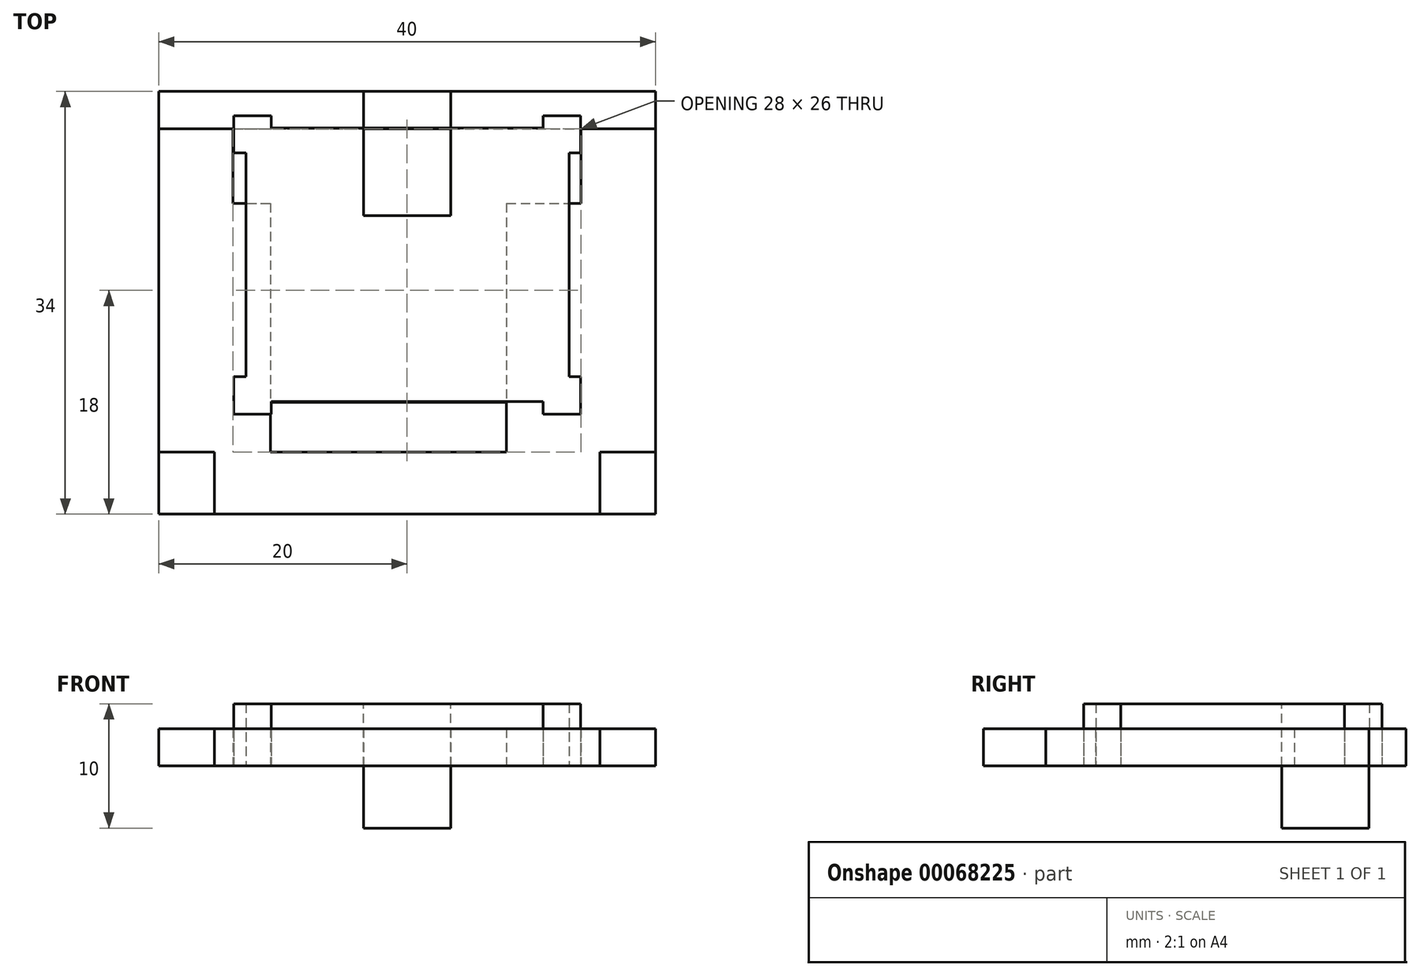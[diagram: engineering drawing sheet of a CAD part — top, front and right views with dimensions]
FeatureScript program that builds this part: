
annotation { "Feature Type Name" : "Feature", "Feature Type Description" : "" }
export const myFeature = defineFeature(function(context is Context, id is Id, definition is map)
    precondition{}
    {
        {
            var Q0;
            Q0=qCreatedBy(makeId("Top.planeOp"),FACE);
            var sketch = newSketch(context, id + "F0", { "sketchPlane" : qUnion([Q0])});
            skLineSegment(sketch, "E0.rect.bottom", {"start": v(-20, 17) * mm, "end": v(20, 17) * mm});
            skLineSegment(sketch, "E0.rect.top", {"start": v(-20, -17) * mm, "end": v(20, -17) * mm});
            skLineSegment(sketch, "E0.rect.left", {"start": v(-20, 17) * mm, "end": v(-20, -17) * mm});
            skLineSegment(sketch, "E0.rect.right", {"start": v(20, 17) * mm, "end": v(20, -17) * mm});
            skPoint(sketch, "E0.rect.middle", {"position": v(0, 0) * mm});
            skLineSegment(sketch, "E1.bottom", {"start": v(-20, -17) * mm, "end": v(-15.5, -17) * mm});
            skLineSegment(sketch, "E1.top", {"start": v(-20, -12) * mm, "end": v(-15.5, -12) * mm});
            skLineSegment(sketch, "E1.left", {"start": v(-20, -17) * mm, "end": v(-20, -12) * mm});
            skLineSegment(sketch, "E1.right", {"start": v(-15.5, -17) * mm, "end": v(-15.5, -12) * mm});
            skLineSegment(sketch, "E2.MirrorCS", {"start": v(15.5, -17) * mm, "end": v(15.5, -12) * mm});
            skLineSegment(sketch, "E3.MirrorCS", {"start": v(20, -17) * mm, "end": v(20, -12) * mm});
            skLineSegment(sketch, "E4.MirrorCS", {"start": v(20, -17) * mm, "end": v(15.5, -17) * mm});
            skLineSegment(sketch, "E5.MirrorCS", {"start": v(20, -12) * mm, "end": v(15.5, -12) * mm});
            skLineSegment(sketch, "E6.bottom", {"start": v(-20, 17) * mm, "end": v(-14, 17) * mm});
            skLineSegment(sketch, "E6.top", {"start": v(-20, 14) * mm, "end": v(-14, 14) * mm});
            skLineSegment(sketch, "E6.left", {"start": v(-20, 17) * mm, "end": v(-20, 14) * mm});
            skLineSegment(sketch, "E6.right", {"start": v(-14, 17) * mm, "end": v(-14, 14) * mm});
            skLineSegment(sketch, "E7.MirrorCS", {"start": v(20, 17) * mm, "end": v(20, 14) * mm});
            skLineSegment(sketch, "E8.MirrorCS", {"start": v(14, 17) * mm, "end": v(14, 14) * mm});
            skLineSegment(sketch, "E9.MirrorCS", {"start": v(20, 14) * mm, "end": v(14, 14) * mm});
            skLineSegment(sketch, "E10.MirrorCS", {"start": v(20, 17) * mm, "end": v(14, 17) * mm});
            skLineSegment(sketch, "E11.MirrorCS", {"start": v(20, 17) * mm, "end": v(-20, 17) * mm});
            skLineSegment(sketch, "E12.bottom", {"start": v(-14, 14) * mm, "end": v(14, 14) * mm});
            skLineSegment(sketch, "E12.top", {"start": v(-14, -12) * mm, "end": v(14, -12) * mm});
            skLineSegment(sketch, "E12.left", {"start": v(-14, 14) * mm, "end": v(-14, -12) * mm});
            skLineSegment(sketch, "E12.right", {"start": v(14, 14) * mm, "end": v(14, -12) * mm});
            skLineSegment(sketch, "E13.top", {"start": v(-14, 8) * mm, "end": v(14, 8) * mm});
            skLineSegment(sketch, "E13.left", {"start": v(-14, -12) * mm, "end": v(-14, 8) * mm});
            skLineSegment(sketch, "E13.right", {"start": v(14, -12) * mm, "end": v(14, 8) * mm});
            skLineSegment(sketch, "E14.bottom", {"start": v(-11, 8) * mm, "end": v(8, 8) * mm});
            skLineSegment(sketch, "E14.top", {"start": v(-11, -12) * mm, "end": v(8, -12) * mm});
            skLineSegment(sketch, "E14.left", {"start": v(-11, 8) * mm, "end": v(-11, -12) * mm});
            skLineSegment(sketch, "E14.right", {"start": v(8, 8) * mm, "end": v(8, -12) * mm});
            skLineSegment(sketch, "E15.bottom", {"start": v(0, 17) * mm, "end": v(-3.5, 17) * mm});
            skLineSegment(sketch, "E15.top", {"start": v(0, 7) * mm, "end": v(-3.5, 7) * mm});
            skLineSegment(sketch, "E15.left", {"start": v(0, 17) * mm, "end": v(0, 7) * mm});
            skLineSegment(sketch, "E15.right", {"start": v(-3.5, 17) * mm, "end": v(-3.5, 7) * mm});
            skLineSegment(sketch, "E16.MirrorCS", {"start": v(0, 17) * mm, "end": v(3.5, 17) * mm});
            skLineSegment(sketch, "E17.MirrorCS", {"start": v(3.5, 17) * mm, "end": v(3.5, 7) * mm});
            skLineSegment(sketch, "E18.MirrorCS", {"start": v(0, 7) * mm, "end": v(3.5, 7) * mm});
            skLineSegment(sketch, "E19.top", {"start": v(-14, -8) * mm, "end": v(14, -8) * mm});
            skLineSegment(sketch, "E19.left", {"start": v(-14, -12) * mm, "end": v(-14, -8) * mm});
            skLineSegment(sketch, "E19.right", {"start": v(14, -12) * mm, "end": v(14, -8) * mm});
            skSolve(sketch);
        }
        {
            var Q0;
            Q0=makeQuery(id+"F0.imprint","IMPRINT",FACE,{"disambiguationData":[TD([[makeQuery(id+"F0.imprint","IMPRINT",EDGE,{"derivedFrom":sQuery(id+"F0.wireOp",EDGE,"E6.top")}),1.0]])]});
            var Q1;
            {var subQ0=sQuery(id+"F0.wireOp",EDGE,"E6.right");Q1=makeQuery(id+"F0.imprint","IMPRINT",FACE,{"disambiguationData":[TD([[makeQuery(id+"F0.imprint","IMPRINT",EDGE,{"derivedFrom":subQ0}),1.0]])]});}
            var Q2;
            {var subQ0=sQuery(id+"F0.wireOp",EDGE,"E8.MirrorCS");Q2=makeQuery(id+"F0.imprint","IMPRINT",FACE,{"disambiguationData":[TD([[makeQuery(id+"F0.imprint","IMPRINT",EDGE,{"derivedFrom":subQ0}),-1.0]])]});}
            var Q3;
            {var subQ0=sQuery(id+"F0.wireOp",EDGE,"E8.MirrorCS");Q3=makeQuery(id+"F0.imprint","IMPRINT",FACE,{"disambiguationData":[TD([[makeQuery(id+"F0.imprint","IMPRINT",EDGE,{"derivedFrom":subQ0}),1.0]])]});}
            var Q4;
            Q4=makeQuery(id+"F0.imprint","IMPRINT",FACE,{"disambiguationData":[TD([[makeQuery(id+"F0.imprint","IMPRINT",EDGE,{"derivedFrom":sQuery(id+"F0.wireOp",EDGE,"E2.MirrorCS")}),-1.0]])]});
            var Q5;
            Q5=makeQuery(id+"F0.imprint","IMPRINT",FACE,{"disambiguationData":[TD([[makeQuery(id+"F0.imprint","IMPRINT",EDGE,{"derivedFrom":sQuery(id+"F0.wireOp",EDGE,"E0.rect.top")}),1.0]])]});
            var Q6;
            Q6=makeQuery(id+"F0.imprint","IMPRINT",FACE,{"disambiguationData":[TD([[makeQuery(id+"F0.imprint","IMPRINT",EDGE,{"derivedFrom":sQuery(id+"F0.wireOp",EDGE,"E1.bottom")}),1.0]])]});
            var Q7;
            {var subQ5=sQuery(id+"F0.wireOp",EDGE,"E19.left");Q7=makeQuery(id+"F0.imprint","IMPRINT",FACE,{"disambiguationData":[TD([[makeQuery(id+"F0.imprint","IMPRINT",EDGE,{"derivedFrom":subQ5}),-1.0]])]});}
            var Q8;
            {var subQ0=sQuery(id+"F0.wireOp",EDGE,"E12.top");var subQ1=sQuery(id+"F0.wireOp",EDGE,"E14.left");var subQ2=makeQuery(id+"F0.imprint","INTERSECT",VERTEX,{"derivedFrom":[subQ1,subQ0]});Q8=makeQuery(id+"F0.imprint","IMPRINT",FACE,{"disambiguationData":[TD([[makeQuery(id+"F0.imprint","IMPRINT",EDGE,{"disambiguationData":[TD([[subQ2,1.0]])],"derivedFrom":subQ1}),1.0]])]});}
            var Q9;
            {var subQ5=sQuery(id+"F0.wireOp",EDGE,"E19.right");Q9=makeQuery(id+"F0.imprint","IMPRINT",FACE,{"disambiguationData":[TD([[makeQuery(id+"F0.imprint","IMPRINT",EDGE,{"derivedFrom":subQ5}),1.0]])]});}
            extrude(context, id + "F1", {"entities" : qUnion([Q0, Q1, Q2, Q3, Q4, Q5, Q6, Q7, Q8, Q9]), "depth" : 3 * mm});
        }
        {
            var Q0;
            {var subQ5=sQuery(id+"F0.wireOp",EDGE,"E16.MirrorCS");Q0=makeQuery(id+"F0.imprint","IMPRINT",FACE,{"disambiguationData":[TD([[makeQuery(id+"F0.imprint","IMPRINT",EDGE,{"derivedFrom":subQ5}),-1.0]])]});}
            var Q1;
            {var subQ5=sQuery(id+"F0.wireOp",EDGE,"E15.bottom");Q1=makeQuery(id+"F0.imprint","IMPRINT",FACE,{"disambiguationData":[TD([[makeQuery(id+"F0.imprint","IMPRINT",EDGE,{"derivedFrom":subQ5}),1.0]])]});}
            var Q2;
            {var subQ0=sQuery(id+"F0.wireOp",EDGE,"E15.right");var subQ1=sQuery(id+"F0.wireOp",EDGE,"E12.bottom");var subQ2=makeQuery(id+"F0.imprint","INTERSECT",VERTEX,{"derivedFrom":[subQ1,subQ0]});Q2=makeQuery(id+"F0.imprint","IMPRINT",FACE,{"disambiguationData":[TD([[makeQuery(id+"F0.imprint","IMPRINT",EDGE,{"disambiguationData":[TD([[subQ2,-1.0]])],"derivedFrom":subQ1}),-1.0]])]});}
            var Q3;
            {var subQ0=sQuery(id+"F0.wireOp",EDGE,"E15.left");var subQ1=sQuery(id+"F0.wireOp",EDGE,"E12.bottom");var subQ2=makeQuery(id+"F0.imprint","INTERSECT",VERTEX,{"derivedFrom":[subQ1,subQ0]});Q3=makeQuery(id+"F0.imprint","IMPRINT",FACE,{"disambiguationData":[TD([[makeQuery(id+"F0.imprint","IMPRINT",EDGE,{"disambiguationData":[TD([[subQ2,-1.0]])],"derivedFrom":subQ1}),-1.0]])]});}
            var Q4;
            {var subQ5=sQuery(id+"F0.wireOp",EDGE,"E18.MirrorCS");Q4=makeQuery(id+"F0.imprint","IMPRINT",FACE,{"disambiguationData":[TD([[makeQuery(id+"F0.imprint","IMPRINT",EDGE,{"derivedFrom":subQ5}),1.0]])]});}
            var Q5;
            {var subQ5=sQuery(id+"F0.wireOp",EDGE,"E15.top");Q5=makeQuery(id+"F0.imprint","IMPRINT",FACE,{"disambiguationData":[TD([[makeQuery(id+"F0.imprint","IMPRINT",EDGE,{"derivedFrom":subQ5}),-1.0]])]});}
            extrude(context, id + "F2", {"entities" : qUnion([Q0, Q1, Q2, Q3, Q4, Q5]), "oppositeDirection" : true, "depth" : 5 * mm, "hasSecondDirection" : true, "secondDirectionOppositeDirection" : false, "secondDirectionDepth" : 5 * mm});
        }
        {
            var Q0;
            Q0=qCreatedBy(makeId("Top.planeOp"),FACE);
            var sketch = newSketch(context, id + "F3", { "sketchPlane" : qUnion([Q0])});
            skPoint(sketch, "E20.rect.middle", {"position": v(0.05, 16.44) * mm});
            skPoint(sketch, "E21.rect.middle", {"position": v(0, 0) * mm});
            skLineSegment(sketch, "E22", {"start": v(0.05, 14.05) * mm, "end": v(0.05, 18.82) * mm, "construction": true});
            skPoint(sketch, "E23", {"position": v(-56.83, 14.05) * mm});
            skPoint(sketch, "E24", {"position": v(56.93, 14.05) * mm});
            skLineSegment(sketch, "E25", {"start": v(-20.06, 17.02) * mm, "end": v(20.05, 17.02) * mm, "construction": true});
            skLineSegment(sketch, "E26.bottom", {"start": v(-12.95, 14.05) * mm, "end": v(13.05, 14.05) * mm});
            skLineSegment(sketch, "E26.top", {"start": v(-12.95, -7.95) * mm, "end": v(13.05, -7.95) * mm});
            skLineSegment(sketch, "E26.left", {"start": v(-12.95, 14.05) * mm, "end": v(-12.95, -7.95) * mm});
            skLineSegment(sketch, "E26.right", {"start": v(13.05, 14.05) * mm, "end": v(13.05, -7.95) * mm});
            skLineSegment(sketch, "E27", {"start": v(-22.7, 3.05) * mm, "end": v(13.05, 3.05) * mm, "construction": true});
            skLineSegment(sketch, "E28.bottom", {"start": v(-13.95, -5.95) * mm, "end": v(-10.95, -5.95) * mm});
            skLineSegment(sketch, "E28.top", {"start": v(-13.95, -8.95) * mm, "end": v(-10.95, -8.95) * mm});
            skLineSegment(sketch, "E28.left", {"start": v(-13.95, -5.95) * mm, "end": v(-13.95, -8.95) * mm});
            skLineSegment(sketch, "E28.right", {"start": v(-10.95, -5.95) * mm, "end": v(-10.95, -8.95) * mm});
            skLineSegment(sketch, "E29.bottom", {"start": v(-10.95, -7.95) * mm, "end": v(-12.95, -7.95) * mm});
            skLineSegment(sketch, "E29.top", {"start": v(-10.95, -5.95) * mm, "end": v(-12.95, -5.95) * mm});
            skLineSegment(sketch, "E29.left", {"start": v(-10.95, -7.95) * mm, "end": v(-10.95, -5.95) * mm});
            skLineSegment(sketch, "E29.right", {"start": v(-12.95, -7.95) * mm, "end": v(-12.95, -5.95) * mm});
            skPoint(sketch, "E30", {"position": v(0.05, 14.05) * mm});
            skLineSegment(sketch, "E31", {"start": v(0.05, 14.05) * mm, "end": v(0.05, -13.67) * mm, "construction": true});
            skPoint(sketch, "E31.endSnap0", {"position": v(0.05, -7.95) * mm});
            skLineSegment(sketch, "E32", {"start": v(0, 17.02) * mm, "end": v(0, -19.93) * mm, "construction": true});
            skLineSegment(sketch, "E33.MirrorCS", {"start": v(-0.06, 14.05) * mm, "end": v(-0.06, -13.67) * mm, "construction": true});
            skLineSegment(sketch, "E34.MirrorCS", {"start": v(10.94, -5.95) * mm, "end": v(12.94, -5.95) * mm});
            skLineSegment(sketch, "E35.MirrorCS", {"start": v(10.94, -7.95) * mm, "end": v(10.94, -5.95) * mm});
            skLineSegment(sketch, "E36.MirrorCS", {"start": v(10.94, -7.95) * mm, "end": v(12.94, -7.95) * mm});
            skLineSegment(sketch, "E37.MirrorCS", {"start": v(12.94, -7.95) * mm, "end": v(12.94, -5.95) * mm});
            skLineSegment(sketch, "E38.MirrorCS", {"start": v(-10.95, 12.05) * mm, "end": v(-12.95, 12.05) * mm});
            skLineSegment(sketch, "E39.MirrorCS", {"start": v(-10.95, 14.05) * mm, "end": v(-10.95, 12.05) * mm});
            skLineSegment(sketch, "E40.MirrorCS", {"start": v(-12.95, 14.05) * mm, "end": v(-12.95, 12.05) * mm});
            skLineSegment(sketch, "E41.MirrorCS", {"start": v(-10.95, 14.05) * mm, "end": v(-12.95, 14.05) * mm});
            skLineSegment(sketch, "E42.MirrorCS", {"start": v(10.94, 12.05) * mm, "end": v(12.94, 12.05) * mm});
            skLineSegment(sketch, "E43.MirrorCS", {"start": v(10.94, 14.05) * mm, "end": v(10.94, 12.05) * mm});
            skLineSegment(sketch, "E44.MirrorCS", {"start": v(10.94, 14.05) * mm, "end": v(12.94, 14.05) * mm});
            skLineSegment(sketch, "E45.MirrorCS", {"start": v(12.94, 14.05) * mm, "end": v(12.94, 12.05) * mm});
            skLineSegment(sketch, "E46.bottom", {"start": v(-10.95, 12.05) * mm, "end": v(-13.95, 12.05) * mm});
            skLineSegment(sketch, "E46.top", {"start": v(-10.95, 15.05) * mm, "end": v(-13.95, 15.05) * mm});
            skLineSegment(sketch, "E46.left", {"start": v(-10.95, 12.05) * mm, "end": v(-10.95, 15.05) * mm});
            skLineSegment(sketch, "E46.right", {"start": v(-13.95, 12.05) * mm, "end": v(-13.95, 15.05) * mm});
            skLineSegment(sketch, "E47.bottom", {"start": v(10.94, 12.05) * mm, "end": v(13.94, 12.05) * mm});
            skLineSegment(sketch, "E47.top", {"start": v(10.94, 15.05) * mm, "end": v(13.94, 15.05) * mm});
            skLineSegment(sketch, "E47.left", {"start": v(10.94, 12.05) * mm, "end": v(10.94, 15.05) * mm});
            skLineSegment(sketch, "E47.right", {"start": v(13.94, 12.05) * mm, "end": v(13.94, 15.05) * mm});
            skLineSegment(sketch, "E48.bottom", {"start": v(10.94, -5.95) * mm, "end": v(13.94, -5.95) * mm});
            skLineSegment(sketch, "E48.top", {"start": v(10.94, -8.95) * mm, "end": v(13.94, -8.95) * mm});
            skLineSegment(sketch, "E48.left", {"start": v(10.94, -5.95) * mm, "end": v(10.94, -8.95) * mm});
            skLineSegment(sketch, "E48.right", {"start": v(13.94, -5.95) * mm, "end": v(13.94, -8.95) * mm});
            skPoint(sketch, "E49", {"position": v(-0.06, 3.1) * mm});
            skLineSegment(sketch, "E50", {"start": v(-13.95, 15.05) * mm, "end": v(13.94, -8.95) * mm, "construction": true});
            skLineSegment(sketch, "E51", {"start": v(-13.95, -8.95) * mm, "end": v(13.94, 15.05) * mm, "construction": true});
            skSolve(sketch);
        }
        {
            var Q0;
            Q0=qSketchRegion(id+"F0",true);
            var Q1;
            {var subQ5=sQuery(id+"F0.wireOp",EDGE,"E12.left");Q1=makeQuery(id+"F0.imprint","IMPRINT",FACE,{"disambiguationData":[TD([[makeQuery(id+"F0.imprint","IMPRINT",EDGE,{"derivedFrom":subQ5}),1.0]])]});}
            var Q2;
            {var subQ5=sQuery(id+"F0.wireOp",EDGE,"E12.right");Q2=makeQuery(id+"F0.imprint","IMPRINT",FACE,{"disambiguationData":[TD([[makeQuery(id+"F0.imprint","IMPRINT",EDGE,{"derivedFrom":subQ5}),-1.0]])]});}
            var Q3;
            {var subQ0=sQuery(id+"F0.wireOp",EDGE,"E13.right");Q3=makeQuery(id+"F0.imprint","IMPRINT",FACE,{"disambiguationData":[TD([[makeQuery(id+"F0.imprint","IMPRINT",EDGE,{"derivedFrom":subQ0}),1.0]])]});}
            var Q4;
            {var subQ0=sQuery(id+"F0.wireOp",EDGE,"E13.left");Q4=makeQuery(id+"F0.imprint","IMPRINT",FACE,{"disambiguationData":[TD([[makeQuery(id+"F0.imprint","IMPRINT",EDGE,{"derivedFrom":subQ0}),-1.0]])]});}
            extrude(context, id + "F4", {"entities" : qUnion([Q0, Q1, Q2, Q3, Q4]), "depth" : 3 * mm});
        }
        {
            var Q0;
            Q0=qSketchRegion(id+"F3",true);
            var Q1;
            Q1=makeQuery(id+"F3.imprint","IMPRINT",FACE,{"disambiguationData":[TD([[makeQuery(id+"F3.imprint","IMPRINT",EDGE,{"derivedFrom":sQuery(id+"F3.wireOp",EDGE,"E21.rect.bottom")}),-1.0]])]});
            extrude(context, id + "F5", {"entities" : qUnion([Q0, Q1]), "depth" : 5 * mm});
        }
    });
